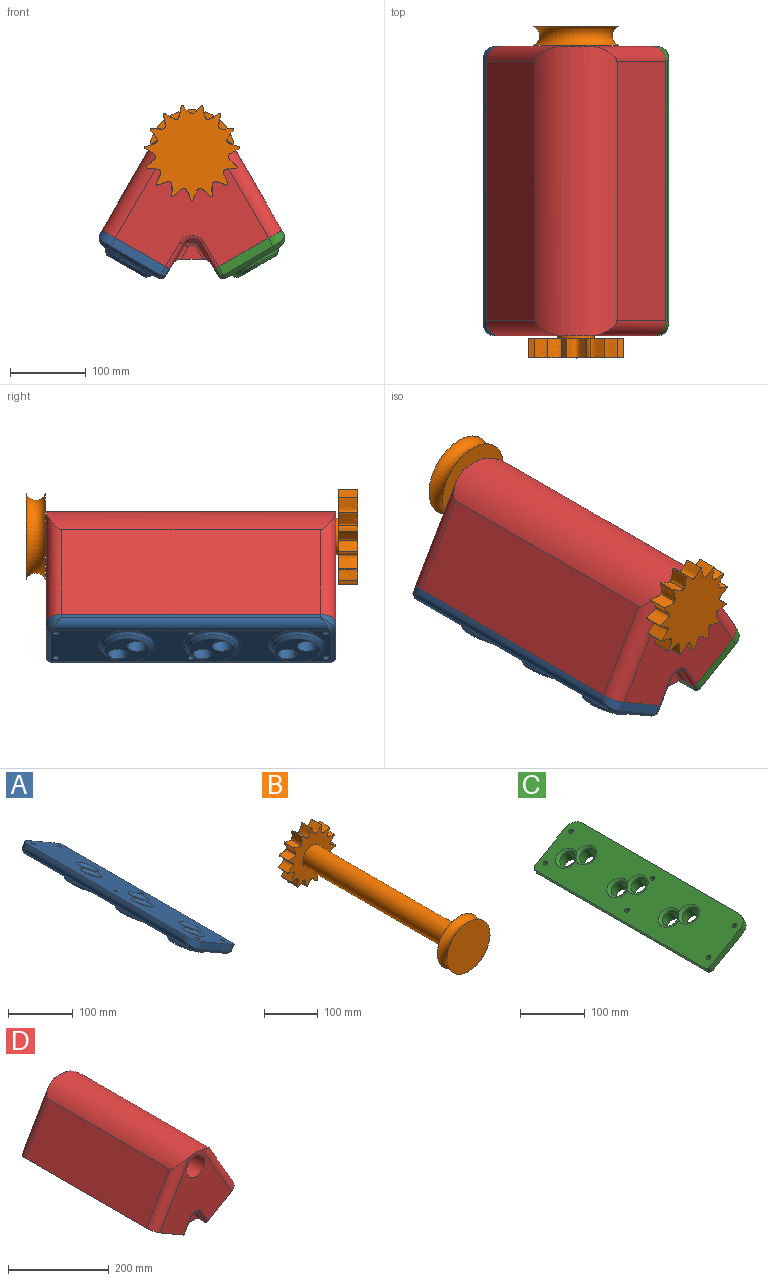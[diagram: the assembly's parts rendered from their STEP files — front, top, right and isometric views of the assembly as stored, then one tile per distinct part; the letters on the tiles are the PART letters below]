
ASSEMBLY  parts=4 mates=3
PART A: 50 faces, bbox 95.2x381x63.8 mm
  f0: plane 72.06x48.54mm, normal (0,-1,0), area 951mm2, adj f2,f31,f32,f40,f41
  f1: plane 368.3x8.64mm, normal (0.87,0,-0.5), area 3674.8mm2, adj f2,f6,f30,f31
  f2: plane 381.01x88.91mm, normal (0.5,0,0.87), area 32771.5mm2, adj f0,f1,f3,f7,f23,f24,f25,f26
  f3: plane 340.36x4.24mm, normal (-0.87,0,0.5), area 1667mm2, adj f2,f4,f32,f33
  f4: cylinder r=12.7mm len=366.76mm, axis (0,1,0), area 7053.2mm2, adj f3,f5,f34,f43
  f5: plane 370.84x71.3mm, normal (-0.5,0,-0.87), area 16567.8mm2, adj f4,f6,f20,f21,f22,f23,f24,f25
  f6: cylinder r=7.62mm len=370.84mm, axis (0,1,0), area 4428.6mm2, adj f1,f5,f37,f38,f39,f40
  f7: plane 72.06x48.54mm, normal (0,1,0), area 951mm2, adj f2,f30,f33,f36,f37
  f8: cylinder r=12.7mm len=32.07mm, axis (-0.5,0,-0.87), area 1606.9mm2, adj f16,f44
  f9: cylinder r=12.7mm len=32.07mm, axis (-0.5,0,-0.87), area 1606.9mm2, adj f14,f48
  f10: cylinder r=12.7mm len=32.07mm, axis (-0.5,0,-0.87), area 1606.9mm2, adj f15,f47
  f11: cylinder r=12.7mm len=32.07mm, axis (-0.5,0,-0.87), area 1606.9mm2, adj f16,f45
  f12: cylinder r=12.7mm len=32.07mm, axis (-0.5,0,-0.87), area 1606.9mm2, adj f15,f46
  f13: cylinder r=12.7mm len=32.07mm, axis (-0.5,0,-0.87), area 1606.9mm2, adj f14,f49
  f14: plane 60.96x52.79mm, normal (-0.5,0,-0.87), area 1905.2mm2, adj f9,f13,f19
  f15: plane 60.96x52.79mm, normal (-0.5,0,-0.87), area 1905.2mm2, adj f10,f12,f18
  f16: plane 60.96x52.79mm, normal (-0.5,0,-0.87), area 1905.2mm2, adj f8,f11,f17
  f17: cone r=30.48mm half-angle=45deg, axis (0.5,0,0.87), area 1096.4mm2, adj f16,f20
  f18: cone r=30.48mm half-angle=45deg, axis (0.5,0,0.87), area 1096.4mm2, adj f15,f22
  f19: cone r=30.48mm half-angle=45deg, axis (0.5,0,0.87), area 1096.4mm2, adj f14,f21
  f20: torus R=38.1mm, axis (-0.5,0,-0.87), area 1341.5mm2, adj f5,f17
  f21: torus R=38.1mm, axis (-0.5,0,-0.87), area 1341.5mm2, adj f5,f19
  f22: torus R=38.1mm, axis (-0.5,0,-0.87), area 1341.5mm2, adj f5,f18,f29
  f23: cylinder r=3.81mm len=19.05mm, axis (-0.5,0,-0.87), area 421.3mm2, adj f2,f5
  f24: cylinder r=3.81mm len=19.05mm, axis (-0.5,0,-0.87), area 421.3mm2, adj f2,f5
  f25: cylinder r=3.81mm len=19.05mm, axis (-0.5,0,-0.87), area 421.3mm2, adj f2,f5
  f26: cylinder r=3.81mm len=19.05mm, axis (-0.5,0,-0.87), area 421.3mm2, adj f2,f5
  f27: cylinder r=3.81mm len=19.05mm, axis (-0.5,0,-0.87), area 421.3mm2, adj f2,f5
  f28: cylinder r=3.81mm len=19.05mm, axis (-0.5,0,-0.87), area 421.3mm2, adj f2,f5,f29
  f29: plane 1.61x1.25mm, normal (0.5,0,0.87), area 0.2mm2, adj f22,f28
  f30: cylinder r=6.35mm len=13.72mm, axis (-0.5,0,-0.87), area 110.5mm2, adj f1,f2,f7,f38
  f31: cylinder r=6.35mm len=13.72mm, axis (-0.5,0,-0.87), area 110.5mm2, adj f0,f1,f2,f39
  f32: cylinder r=20.32mm len=23.86mm, axis (-0.5,0,-0.87), area 318.5mm2, adj f0,f2,f3,f42,f43
  f33: cylinder r=20.32mm len=23.86mm, axis (-0.5,0,-0.87), area 318.5mm2, adj f2,f3,f7,f34,f35
  f34: bspline ~17.6x17.35mm, area 62.2mm2, adj f4,f33,f35
  f35: cone r=15.24mm half-angle=45deg, axis (0.5,0,0.87), area 66.9mm2, adj f5,f33,f34,f36
  f36: plane 67.24x41.76mm, normal (-0.35,0.71,-0.61), area 536.8mm2, adj f5,f7,f35,f37
  f37: cone r=2.54mm half-angle=45deg, axis (0,-1,0), area 19.1mm2, adj f6,f7,f36,f38
  f38: bspline ~6.6x6.35mm, area 23.8mm2, adj f6,f30,f37
  f39: bspline ~6.6x6.35mm, area 23.8mm2, adj f6,f31,f40
  f40: cone r=2.54mm half-angle=45deg, axis (0,1,0), area 19.1mm2, adj f0,f6,f39,f41
  f41: plane 67.24x41.76mm, normal (-0.35,-0.71,-0.61), area 536.8mm2, adj f0,f5,f40,f42
  f42: cone r=15.24mm half-angle=45deg, axis (0.5,0,0.87), area 66.9mm2, adj f5,f32,f41,f43
  f43: bspline ~17.6x17.35mm, area 62.2mm2, adj f4,f32,f42
  f44: bspline ~35.54x30.76mm, area 726.4mm2, adj f2,f8,f45
  f45: bspline ~35.56x30.8mm, area 726.4mm2, adj f2,f11,f44
  f46: bspline ~35.56x30.8mm, area 726.4mm2, adj f2,f12,f47
  f47: bspline ~35.54x30.76mm, area 726.4mm2, adj f2,f10,f46
  f48: bspline ~35.54x30.76mm, area 726.4mm2, adj f2,f9,f49
  f49: bspline ~35.54x30.76mm, area 726.4mm2, adj f2,f13,f48
PART B: 39 faces, bbox 133.3x437.9x133.3 mm
  f0: cylinder r=63.5mm len=25.4mm, axis (0,1,0), area 5.7mm2, adj f6,f7,f10,f34
  f1: cylinder r=63.5mm len=25.4mm, axis (0,1,0), area 5.7mm2, adj f6,f7,f13,f34
  f2: plane 112.95x112.95mm, normal (0,-1,0), area 10020.7mm2, adj f3
  f3: torus R=61.56mm, axis (0,1,0), area 10411.4mm2, adj f2,f4
  f4: plane 112.95x112.95mm, normal (0,1,0), area 8191.5mm2, adj f3,f5
  f5: cylinder r=24.13mm len=386.08mm, axis (0,1,0), area 58534.8mm2, adj f4,f6
  f6: plane 126.81x125.82mm, normal (0,-1,0), area 7434.3mm2, adj f0,f1,f5,f8,f9,f10,f11,f12
  f7: plane 126.81x125.82mm, normal (0,1,0), area 9263.5mm2, adj f0,f1,f8,f9,f10,f11,f12,f13
  f8: extruded ~25.4x17.69mm, area 500.3mm2, adj f6,f7,f9,f29
  f9: extruded ~25.4x0.09mm, area 2.4mm2, adj f6,f7,f8,f10
  f10: extruded ~25.4x17.99mm, area 498.5mm2, adj f0,f6,f7,f9
  f11: extruded ~25.4x0.09mm, area 2.4mm2, adj f6,f7,f12,f13
  f12: extruded ~25.4x17.69mm, area 500.5mm2, adj f6,f7,f11,f35
  f13: extruded ~25.4x17.99mm, area 498.5mm2, adj f1,f6,f7,f11
  f14: extruded ~25.4x18.6mm, area 501.1mm2, adj f6,f7,f15,f25
  f15: extruded ~25.4x18.36mm, area 501.1mm2, adj f6,f7,f14,f37
  f16: extruded ~25.4x16.84mm, area 501.2mm2, adj f6,f7,f17,f36
  f17: extruded ~25.4x17.25mm, area 501.1mm2, adj f6,f7,f16,f24
  f18: extruded ~25.4x18.97mm, area 501.1mm2, adj f6,f7,f19,f23
  f19: extruded ~25.4x18.82mm, area 501.1mm2, adj f6,f7,f18,f32
  f20: extruded ~25.4x17.25mm, area 501.1mm2, adj f6,f7,f21,f27
  f21: extruded ~25.4x16.84mm, area 501.2mm2, adj f6,f7,f20,f28
  f22: extruded ~25.4x16.29mm, area 501.1mm2, adj f6,f7,f23,f31
  f23: extruded ~25.4x15.79mm, area 501.1mm2, adj f6,f7,f18,f22
  f24: extruded ~25.4x15.16mm, area 501.1mm2, adj f6,f7,f17,f25
  f25: extruded ~25.4x14.58mm, area 501.1mm2, adj f6,f7,f14,f24
  f26: extruded ~25.4x14.58mm, area 501.1mm2, adj f6,f7,f27,f33
  f27: extruded ~25.4x15.16mm, area 501.1mm2, adj f6,f7,f20,f26
  f28: extruded ~25.4x19.13mm, area 501.2mm2, adj f6,f7,f21,f29
  f29: extruded ~25.4x19.08mm, area 501.2mm2, adj f6,f7,f8,f28
  f30: extruded ~25.4x15.79mm, area 501.1mm2, adj f6,f7,f31,f38
  f31: extruded ~25.4x16.29mm, area 501.1mm2, adj f6,f7,f22,f30
  f32: extruded ~25.4x18.36mm, area 501.1mm2, adj f6,f7,f19,f33
  f33: extruded ~25.4x18.6mm, area 501.1mm2, adj f6,f7,f26,f32
  f34: extruded ~25.97x25.4mm, area 880.2mm2, adj f0,f1,f6,f7
  f35: extruded ~25.4x19.08mm, area 501.1mm2, adj f6,f7,f12,f36
  f36: extruded ~25.4x19.13mm, area 501.2mm2, adj f6,f7,f16,f35
  f37: extruded ~25.4x18.82mm, area 501.1mm2, adj f6,f7,f15,f38
  f38: extruded ~25.4x18.97mm, area 501.1mm2, adj f6,f7,f30,f37
PART C: 50 faces, bbox 95.2x381x65.7 mm
  f0: plane 72.06x48.54mm, normal (0,-1,0), area 951mm2, adj f5,f31,f32,f40,f41
  f1: plane 340.36x4.24mm, normal (0.87,0,0.5), area 1667mm2, adj f2,f5,f30,f31
  f2: cylinder r=12.7mm len=366.76mm, axis (0,1,0), area 7053.2mm2, adj f1,f7,f34,f43
  f3: cylinder r=7.62mm len=370.84mm, axis (0,1,0), area 4428.6mm2, adj f4,f7,f37,f38,f39,f40
  f4: plane 368.3x8.64mm, normal (-0.87,0,-0.5), area 3674.8mm2, adj f3,f5,f32,f33
  f5: plane 381.01x88.91mm, normal (-0.5,0,0.87), area 32771.6mm2, adj f0,f1,f4,f6,f23,f24,f26,f27
  f6: plane 72.06x48.54mm, normal (0,1,0), area 951mm2, adj f5,f30,f33,f36,f37
  f7: plane 370.84x71.3mm, normal (0.5,0,-0.87), area 16567.8mm2, adj f2,f3,f20,f21,f22,f23,f24,f26
  f8: cylinder r=12.7mm len=32.07mm, axis (0.5,0,-0.87), area 1606.9mm2, adj f14,f48
  f9: cylinder r=12.7mm len=32.07mm, axis (0.5,0,-0.87), area 1606.9mm2, adj f16,f44
  f10: cylinder r=12.7mm len=32.07mm, axis (0.5,0,-0.87), area 1606.9mm2, adj f16,f45
  f11: cylinder r=12.7mm len=32.07mm, axis (0.5,0,-0.87), area 1606.9mm2, adj f15,f46
  f12: cylinder r=12.7mm len=32.07mm, axis (0.5,0,-0.87), area 1606.9mm2, adj f15,f47
  f13: cylinder r=12.7mm len=32.07mm, axis (0.5,0,-0.87), area 1606.9mm2, adj f14,f49
  f14: plane 60.96x52.79mm, normal (0.5,0,-0.87), area 1905.2mm2, adj f8,f13,f19
  f15: plane 60.96x52.79mm, normal (0.5,0,-0.87), area 1905.2mm2, adj f11,f12,f18
  f16: plane 60.96x52.79mm, normal (0.5,0,-0.87), area 1905.2mm2, adj f9,f10,f17
  f17: cone r=30.48mm half-angle=45deg, axis (-0.5,0,0.87), area 1096.4mm2, adj f16,f20
  f18: cone r=30.48mm half-angle=45deg, axis (-0.5,0,0.87), area 1096.4mm2, adj f15,f21
  f19: cone r=30.48mm half-angle=45deg, axis (-0.5,0,0.87), area 1096.4mm2, adj f14,f22
  f20: torus R=38.1mm, axis (-0.5,0,0.87), area 1341.5mm2, adj f7,f17
  f21: torus R=38.1mm, axis (-0.5,0,0.87), area 1341.5mm2, adj f7,f18,f25
  f22: torus R=38.1mm, axis (-0.5,0,0.87), area 1341.5mm2, adj f7,f19
  f23: cylinder r=3.81mm len=19.05mm, axis (0.5,0,-0.87), area 421.3mm2, adj f5,f7
  f24: cylinder r=3.81mm len=19.05mm, axis (0.5,0,-0.87), area 421.3mm2, adj f5,f7,f25
  f25: plane 1.61x1.25mm, normal (-0.5,0,0.87), area 0.2mm2, adj f21,f24
  f26: cylinder r=3.81mm len=19.05mm, axis (0.5,0,-0.87), area 421.3mm2, adj f5,f7
  f27: cylinder r=3.81mm len=19.05mm, axis (0.5,0,-0.87), area 421.3mm2, adj f5,f7
  f28: cylinder r=3.81mm len=19.05mm, axis (0.5,0,-0.87), area 421.3mm2, adj f5,f7
  f29: cylinder r=3.81mm len=19.05mm, axis (0.5,0,-0.87), area 421.3mm2, adj f5,f7
  f30: cylinder r=20.32mm len=23.86mm, axis (0.5,0,-0.87), area 318.5mm2, adj f1,f5,f6,f34,f35
  f31: cylinder r=20.32mm len=23.86mm, axis (0.5,0,-0.87), area 318.5mm2, adj f0,f1,f5,f42,f43
  f32: cylinder r=6.35mm len=13.72mm, axis (0.5,0,-0.87), area 110.5mm2, adj f0,f4,f5,f39
  f33: cylinder r=6.35mm len=13.72mm, axis (0.5,0,-0.87), area 110.5mm2, adj f4,f5,f6,f38
  f34: bspline ~17.6x17.35mm, area 62.2mm2, adj f2,f30,f35
  f35: cone r=15.24mm half-angle=45deg, axis (-0.5,0,0.87), area 66.9mm2, adj f7,f30,f34,f36
  f36: plane 67.24x41.76mm, normal (0.35,0.71,-0.61), area 536.8mm2, adj f6,f7,f35,f37
  f37: cone r=7.62mm half-angle=45deg, axis (0,-1,0), area 19.1mm2, adj f3,f6,f36,f38
  f38: bspline ~6.6x6.35mm, area 23.8mm2, adj f3,f33,f37
  f39: bspline ~6.6x6.35mm, area 23.8mm2, adj f3,f32,f40
  f40: cone r=7.62mm half-angle=45deg, axis (0,1,0), area 19.1mm2, adj f0,f3,f39,f41
  f41: plane 67.24x41.76mm, normal (0.35,-0.71,-0.61), area 536.8mm2, adj f0,f7,f40,f42
  f42: cone r=15.24mm half-angle=45deg, axis (-0.5,0,0.87), area 66.9mm2, adj f7,f31,f41,f43
  f43: bspline ~17.6x17.35mm, area 62.2mm2, adj f2,f31,f42
  f44: bspline ~35.54x30.76mm, area 726.4mm2, adj f5,f9,f45
  f45: bspline ~35.56x30.8mm, area 726.4mm2, adj f5,f10,f44
  f46: bspline ~35.54x30.76mm, area 726.4mm2, adj f5,f11,f47
  f47: bspline ~35.56x30.8mm, area 726.4mm2, adj f5,f12,f46
  f48: bspline ~35.54x30.76mm, area 726.4mm2, adj f5,f8,f49
  f49: bspline ~35.54x30.76mm, area 726.4mm2, adj f5,f13,f48
PART D: 135 faces, bbox 236.4x381x194.3 mm
  f0: cylinder r=25.4mm len=381mm, axis (0,1,0), area 48366.5mm2, adj f2,f4,f6,f8,f10,f12,f14,f18
  f1: plane 38.34x25.4mm, normal (0.87,0,-0.5), area 1124.5mm2, adj f2,f4,f27,f29,f31,f50
  f2: plane 65.68x62.95mm, normal (0,-1,0), area 1189.4mm2, adj f0,f1,f3,f50
  f3: plane 38.34x25.4mm, normal (-0.87,0,0.5), area 1124.5mm2, adj f2,f4,f28,f30,f32,f50
  f4: plane 65.68x62.95mm, normal (0,1,0), area 1189.4mm2, adj f0,f1,f3,f50
  f5: plane 38.34x25.4mm, normal (0.87,0,-0.5), area 1124.5mm2, adj f6,f8,f33,f35,f37,f48
  f6: plane 65.68x62.95mm, normal (0,-1,0), area 1189.4mm2, adj f0,f5,f7,f48
  f7: plane 38.34x25.4mm, normal (-0.87,0,0.5), area 1124.5mm2, adj f6,f8,f34,f36,f38,f48
  f8: plane 65.68x62.95mm, normal (0,1,0), area 1189.4mm2, adj f0,f5,f7,f48
  f9: plane 38.34x25.4mm, normal (0.87,0,-0.5), area 1124.5mm2, adj f10,f12,f39,f41,f43,f46
  f10: plane 65.68x62.95mm, normal (0,-1,0), area 1189.4mm2, adj f0,f9,f11,f46
  f11: plane 38.34x25.4mm, normal (-0.87,0,0.5), area 1124.5mm2, adj f10,f12,f40,f42,f44,f46
  f12: plane 65.68x62.95mm, normal (0,1,0), area 1189.4mm2, adj f0,f9,f11,f46
  f13: plane 381x88.9mm, normal (-0.5,0,-0.87), area 27560.9mm2, adj f14,f18,f19,f20,f45,f47,f49,f94
  f14: plane 201.21x183.25mm, normal (0,-1,0), area 18290.4mm2, adj f0,f13,f22,f24,f87,f88,f90,f92
  f15: cylinder r=10.16mm len=368.3mm, axis (0,1,0), area 3840.7mm2, adj f16,f20,f96,f104
  f16: plane 355.86x32.21mm, normal (0,0,-1), area 11452.7mm2, adj f15,f17,f25,f26,f89,f96,f97,f104
  f17: cylinder r=10.16mm len=368.3mm, axis (0,1,0), area 3840.7mm2, adj f16,f21,f89,f97
  f18: plane 201.21x183.25mm, normal (0,1,0), area 18290.4mm2, adj f0,f13,f22,f24,f99,f101,f103,f105
  f19: plane 340.36x111.23mm, normal (-0.87,0,0.5), area 43716.3mm2, adj f13,f24,f107,f110
  f20: plane 368.3x7.62mm, normal (0.87,0,-0.5), area 3240.6mm2, adj f13,f15,f94,f106
  f21: plane 368.3x7.62mm, normal (-0.87,0,-0.5), area 3240.6mm2, adj f17,f22,f87,f99
  f22: plane 381x88.9mm, normal (0.5,0,-0.87), area 27560.9mm2, adj f14,f18,f21,f23,f51,f53,f55,f87
  f23: plane 340.36x111.23mm, normal (0.87,0,0.5), area 43716.3mm2, adj f22,f24,f108,f109
  f24: cylinder r=72.98mm len=381mm, axis (0,1,0), area 45293.6mm2, adj f14,f18,f19,f23,f107,f108,f109,f110
  f25: plane 29.27x18.5mm, normal (0,1,0), area 342.4mm2, adj f16,f97,f98,f100,f102,f104
  f26: plane 29.27x18.5mm, normal (0,-1,0), area 342.4mm2, adj f16,f89,f91,f93,f95,f96
  f27: plane 25.4x0.01mm, normal (-0.5,0,-0.87), area 0.4mm2, adj f0,f1,f29,f31
  f28: plane 25.4x0.01mm, normal (-0.5,0,-0.87), area 0.4mm2, adj f0,f3,f30,f32
  f29: plane 0.79x0.47mm, normal (0,-1,0), area 0mm2, adj f0,f1,f27
  f30: plane 0.8x0.46mm, normal (0,-1,0), area 0mm2, adj f0,f3,f28
  f31: plane 0.79x0.47mm, normal (0,1,0), area 0mm2, adj f0,f1,f27
  f32: plane 0.8x0.46mm, normal (0,1,0), area 0mm2, adj f0,f3,f28
  f33: plane 25.4x0.01mm, normal (-0.5,0,-0.87), area 0.4mm2, adj f0,f5,f35,f37
  f34: plane 25.4x0.01mm, normal (-0.5,0,-0.87), area 0.4mm2, adj f0,f7,f36,f38
  f35: plane 0.79x0.47mm, normal (0,-1,0), area 0mm2, adj f0,f5,f33
  f36: plane 0.8x0.46mm, normal (0,-1,0), area 0mm2, adj f0,f7,f34
  f37: plane 0.79x0.47mm, normal (0,1,0), area 0mm2, adj f0,f5,f33
  f38: plane 0.8x0.46mm, normal (0,1,0), area 0mm2, adj f0,f7,f34
  f39: plane 25.4x0.01mm, normal (-0.5,0,-0.87), area 0.4mm2, adj f0,f9,f41,f43
  f40: plane 25.4x0.01mm, normal (-0.5,0,-0.87), area 0.4mm2, adj f0,f11,f42,f44
  f41: plane 0.79x0.47mm, normal (0,-1,0), area 0mm2, adj f0,f9,f39
  f42: plane 0.8x0.46mm, normal (0,-1,0), area 0mm2, adj f0,f11,f40
  f43: plane 0.79x0.47mm, normal (0,1,0), area 0mm2, adj f0,f9,f39
  f44: plane 0.8x0.46mm, normal (0,1,0), area 0mm2, adj f0,f11,f40
  f45: cone r=34.29mm half-angle=3deg, axis (0.5,0,0.87), area 24255.8mm2, adj f13,f46
  f46: plane 79.5x68.85mm, normal (-0.5,0,-0.87), area 3673mm2, adj f9,f10,f11,f12,f45
  f47: cone r=34.29mm half-angle=3deg, axis (0.5,0,0.87), area 24255.8mm2, adj f13,f48
  f48: plane 79.5x68.85mm, normal (-0.5,0,-0.87), area 3673mm2, adj f5,f6,f7,f8,f47
  f49: cone r=34.29mm half-angle=3deg, axis (0.5,0,0.87), area 24255.8mm2, adj f13,f50
  f50: plane 79.5x68.85mm, normal (-0.5,0,-0.87), area 3673mm2, adj f1,f2,f3,f4,f49
  f51: cylinder r=34.29mm len=124.48mm, axis (0.5,0,-0.87), area 22437mm2, adj f22,f52
  f52: plane 68.58x59.39mm, normal (0.5,0,-0.87), area 2403.6mm2, adj f51,f81,f82,f85,f86
  f53: cylinder r=34.29mm len=124.48mm, axis (0.5,0,-0.87), area 22437mm2, adj f22,f54
  f54: plane 68.58x59.39mm, normal (0.5,0,-0.87), area 2403.6mm2, adj f53,f71,f72,f75,f76
  f55: cylinder r=34.29mm len=124.48mm, axis (0.5,0,-0.87), area 22437mm2, adj f22,f56
  f56: plane 68.58x59.39mm, normal (0.5,0,-0.87), area 2403.6mm2, adj f55,f59,f62,f63,f66
  f57: plane 25.4x0.01mm, normal (0.5,0,-0.87), area 0.4mm2, adj f0,f60,f63,f64
  f58: plane 25.4x0.01mm, normal (0.5,0,-0.87), area 0.4mm2, adj f0,f59,f61,f65
  f59: plane 38.34x25.4mm, normal (-0.87,0,-0.5), area 1124.5mm2, adj f56,f58,f61,f62,f65,f66
  f60: plane 0.8x0.46mm, normal (0,1,0), area 0mm2, adj f0,f57,f63
  f61: plane 0.79x0.47mm, normal (0,1,0), area 0mm2, adj f0,f58,f59
  f62: plane 65.68x62.95mm, normal (0,1,0), area 1189.4mm2, adj f0,f56,f59,f63
  f63: plane 38.34x25.4mm, normal (0.87,0,0.5), area 1124.5mm2, adj f56,f57,f60,f62,f64,f66
  f64: plane 0.8x0.46mm, normal (0,-1,0), area 0mm2, adj f0,f57,f63
  f65: plane 0.79x0.47mm, normal (0,-1,0), area 0mm2, adj f0,f58,f59
  f66: plane 65.68x62.95mm, normal (0,-1,0), area 1189.4mm2, adj f0,f56,f59,f63
  f67: plane 25.4x0.01mm, normal (0.5,0,-0.87), area 0.4mm2, adj f0,f69,f72,f73
  f68: plane 25.4x0.01mm, normal (0.5,0,-0.87), area 0.4mm2, adj f0,f70,f74,f76
  f69: plane 0.8x0.46mm, normal (0,1,0), area 0mm2, adj f0,f67,f72
  f70: plane 0.79x0.47mm, normal (0,1,0), area 0mm2, adj f0,f68,f76
  f71: plane 65.68x62.95mm, normal (0,1,0), area 1189.4mm2, adj f0,f54,f72,f76
  f72: plane 38.34x25.4mm, normal (0.87,0,0.5), area 1124.5mm2, adj f54,f67,f69,f71,f73,f75
  f73: plane 0.8x0.46mm, normal (0,-1,0), area 0mm2, adj f0,f67,f72
  f74: plane 0.79x0.47mm, normal (0,-1,0), area 0mm2, adj f0,f68,f76
  f75: plane 65.68x62.95mm, normal (0,-1,0), area 1189.4mm2, adj f0,f54,f72,f76
  f76: plane 38.34x25.4mm, normal (-0.87,0,-0.5), area 1124.5mm2, adj f54,f68,f70,f71,f74,f75
  f77: plane 25.4x0.01mm, normal (0.5,0,-0.87), area 0.4mm2, adj f0,f79,f82,f83
  f78: plane 25.4x0.01mm, normal (0.5,0,-0.87), area 0.4mm2, adj f0,f80,f84,f86
  f79: plane 0.8x0.46mm, normal (0,1,0), area 0mm2, adj f0,f77,f82
  f80: plane 0.79x0.47mm, normal (0,1,0), area 0mm2, adj f0,f78,f86
  f81: plane 65.68x62.95mm, normal (0,1,0), area 1189.4mm2, adj f0,f52,f82,f86
  f82: plane 38.34x25.4mm, normal (0.87,0,0.5), area 1124.5mm2, adj f52,f77,f79,f81,f83,f85
  f83: plane 0.8x0.46mm, normal (0,-1,0), area 0mm2, adj f0,f77,f82
  f84: plane 0.79x0.47mm, normal (0,-1,0), area 0mm2, adj f0,f78,f86
  f85: plane 65.68x62.95mm, normal (0,-1,0), area 1189.4mm2, adj f0,f52,f82,f86
  f86: plane 38.34x25.4mm, normal (-0.87,0,-0.5), area 1124.5mm2, adj f52,f78,f80,f81,f84,f85
  f87: cylinder r=6.35mm len=35.65mm, axis (0.5,0,-0.87), area 374mm2, adj f14,f21,f22,f88,f89
  f88: torus R=16.51mm, axis (0,-1,0), area 130.2mm2, adj f14,f87,f90,f91
  f89: cylinder r=6.35mm len=28.03mm, axis (-0.5,0,0.87), area 231.7mm2, adj f16,f17,f26,f87,f91
  f90: cylinder r=6.35mm len=6.35mm, axis (-1,0,0), area 35mm2, adj f14,f88,f92,f93
  f91: torus R=3.81mm, axis (0,1,0), area 82mm2, adj f26,f88,f89,f93
  f92: torus R=16.51mm, axis (0,-1,0), area 130.2mm2, adj f14,f90,f94,f95
  f93: cylinder r=6.35mm len=6.35mm, axis (-1,0,0), area 35mm2, adj f26,f90,f91,f95
  f94: cylinder r=6.35mm len=35.65mm, axis (0.5,0,0.87), area 374mm2, adj f13,f14,f20,f92,f96
  f95: torus R=3.81mm, axis (0,1,0), area 82mm2, adj f26,f92,f93,f96
  f96: cylinder r=6.35mm len=28.03mm, axis (-0.5,0,-0.87), area 231.7mm2, adj f15,f16,f26,f94,f95
  f97: cylinder r=6.35mm len=28.03mm, axis (0.5,0,-0.87), area 231.7mm2, adj f16,f17,f25,f98,f99
  f98: torus R=3.81mm, axis (0,1,0), area 82mm2, adj f25,f97,f100,f101
  f99: cylinder r=6.35mm len=35.65mm, axis (0.5,0,-0.87), area 374mm2, adj f18,f21,f22,f97,f101
  f100: cylinder r=6.35mm len=6.35mm, axis (1,0,0), area 35mm2, adj f25,f98,f102,f103
  f101: torus R=16.51mm, axis (0,-1,0), area 130.2mm2, adj f18,f98,f99,f103
  f102: torus R=3.81mm, axis (0,1,0), area 82mm2, adj f25,f100,f104,f105
  f103: cylinder r=6.35mm len=6.35mm, axis (1,0,0), area 35mm2, adj f18,f100,f101,f105
  f104: cylinder r=6.35mm len=28.03mm, axis (0.5,0,0.87), area 231.7mm2, adj f15,f16,f25,f102,f106
  f105: torus R=16.51mm, axis (0,-1,0), area 130.2mm2, adj f18,f102,f103,f106
  f106: cylinder r=6.35mm len=35.65mm, axis (0.5,0,0.87), area 374mm2, adj f13,f18,f20,f104,f105
  f107: cylinder r=20.32mm len=153.15mm, axis (-0.5,0,-0.87), area 4644.3mm2, adj f13,f14,f19,f24
  f108: cylinder r=20.32mm len=153.15mm, axis (-0.5,0,0.87), area 4644.3mm2, adj f14,f22,f23,f24
  f109: cylinder r=20.32mm len=153.15mm, axis (-0.5,0,0.87), area 4644.3mm2, adj f18,f22,f23,f24
  f110: cylinder r=20.32mm len=153.15mm, axis (-0.5,0,-0.87), area 4644.3mm2, adj f13,f18,f19,f24
  f111: cylinder r=3.81mm len=47.8mm, axis (0.5,0,-0.87), area 1216.1mm2, adj f22,f112
  f112: plane 7.62x6.6mm, normal (0.5,0,-0.87), area 45.6mm2, adj f111
  f113: cylinder r=3.81mm len=47.8mm, axis (0.5,0,-0.87), area 1216.1mm2, adj f22,f114
  f114: plane 7.62x6.6mm, normal (0.5,0,-0.87), area 45.6mm2, adj f113
  f115: cylinder r=3.81mm len=47.8mm, axis (0.5,0,-0.87), area 1216.1mm2, adj f22,f116
  f116: plane 7.62x6.6mm, normal (0.5,0,-0.87), area 45.6mm2, adj f115
  f117: cylinder r=3.81mm len=47.8mm, axis (0.5,0,-0.87), area 1216.1mm2, adj f22,f118
  f118: plane 7.62x6.6mm, normal (0.5,0,-0.87), area 45.6mm2, adj f117
  f119: cylinder r=3.81mm len=47.8mm, axis (0.5,0,-0.87), area 1216.1mm2, adj f22,f120
  f120: plane 7.62x6.6mm, normal (0.5,0,-0.87), area 45.6mm2, adj f119
  f121: cylinder r=3.81mm len=47.8mm, axis (0.5,0,-0.87), area 1216.1mm2, adj f22,f122
  f122: plane 7.62x6.6mm, normal (0.5,0,-0.87), area 45.6mm2, adj f121
  f123: cylinder r=3.81mm len=47.8mm, axis (-0.5,0,-0.87), area 1216.1mm2, adj f13,f124
  f124: plane 7.62x6.6mm, normal (-0.5,0,-0.87), area 45.6mm2, adj f123
  f125: cylinder r=3.81mm len=47.8mm, axis (-0.5,0,-0.87), area 1216.1mm2, adj f13,f126
  f126: plane 7.62x6.6mm, normal (-0.5,0,-0.87), area 45.6mm2, adj f125
  f127: cylinder r=3.81mm len=47.8mm, axis (-0.5,0,-0.87), area 1216.1mm2, adj f13,f128
  f128: plane 7.62x6.6mm, normal (-0.5,0,-0.87), area 45.6mm2, adj f127
  f129: cylinder r=3.81mm len=47.8mm, axis (-0.5,0,-0.87), area 1216.1mm2, adj f13,f130
  f130: plane 7.62x6.6mm, normal (-0.5,0,-0.87), area 45.6mm2, adj f129
  f131: cylinder r=3.81mm len=47.8mm, axis (-0.5,0,-0.87), area 1216.1mm2, adj f13,f132
  f132: plane 7.62x6.6mm, normal (-0.5,0,-0.87), area 45.6mm2, adj f131
  f133: cylinder r=3.81mm len=47.8mm, axis (-0.5,0,-0.87), area 1216.1mm2, adj f13,f134
  f134: plane 7.62x6.6mm, normal (-0.5,0,-0.87), area 45.6mm2, adj f133
PLACE A t=(25.95,54.12,-173.43)mm
PLACE B rot(axis=(1,0,0),180deg) t=(25.95,116.35,-4.78)mm
PLACE C t=(25.95,54.12,-173.43)mm
PLACE D t=(25.95,54.12,-173.43)mm
MATE revolute B.f0 <-> D.f0  axis (0,-1,0) through (25.95,309.39,-4.78)mm
MATE fastened D.f123 <-> A.f23  axis (-0.5,0,-0.87) through (-74.65,-60.18,-117.02)mm
MATE fastened C.f23 <-> D.f111  axis (-0.5,0,0.87) through (126.55,-60.18,-117.02)mm
